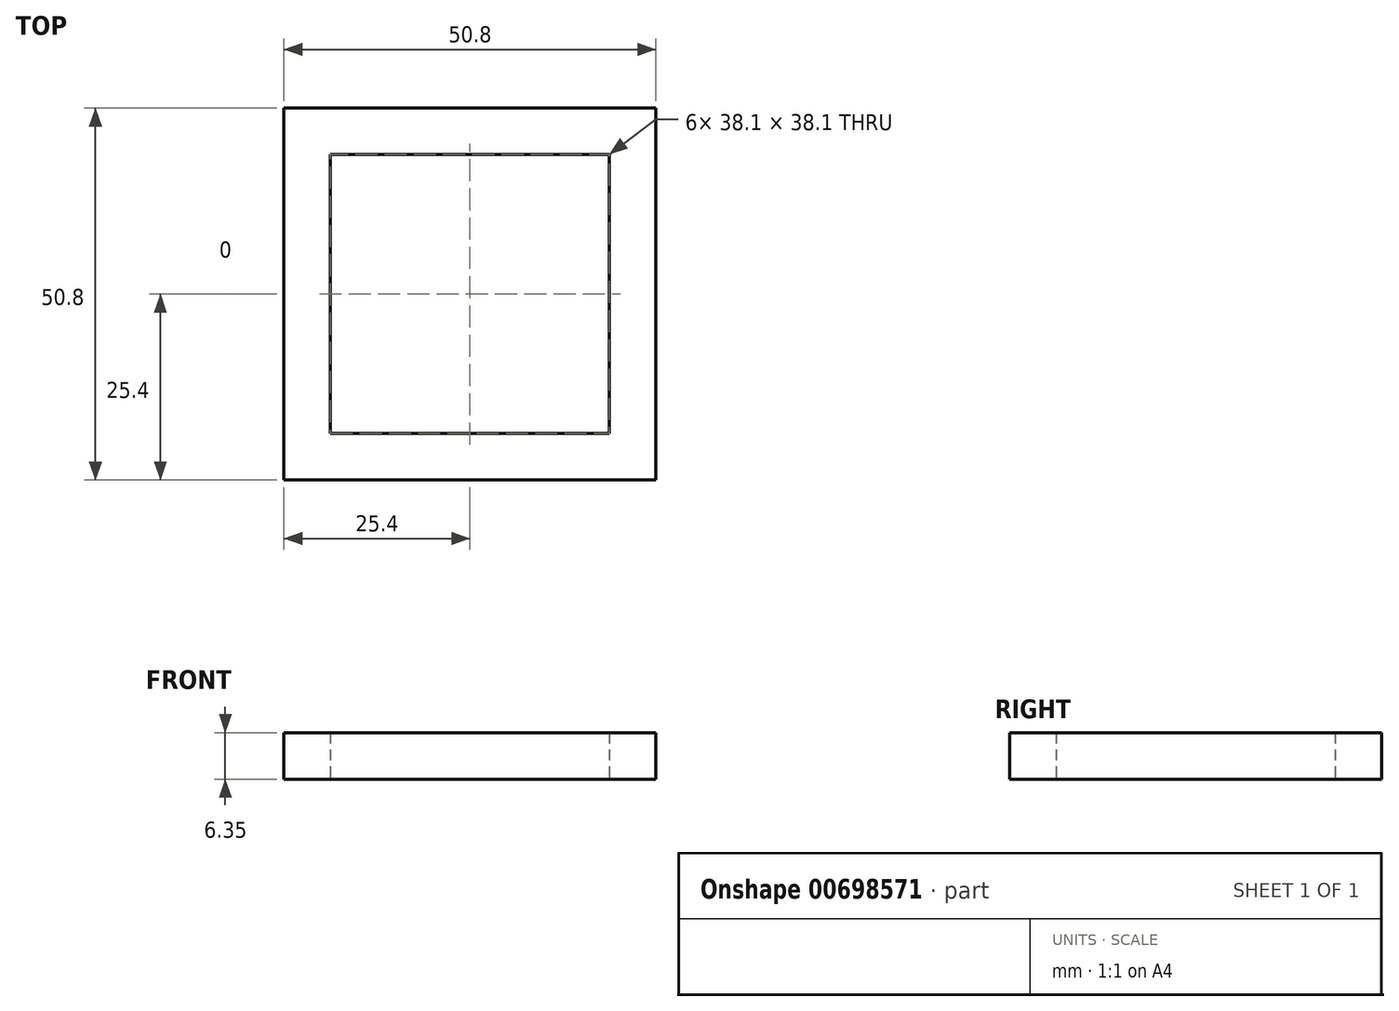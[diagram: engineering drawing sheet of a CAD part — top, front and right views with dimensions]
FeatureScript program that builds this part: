
annotation { "Feature Type Name" : "Feature", "Feature Type Description" : "" }
export const myFeature = defineFeature(function(context is Context, id is Id, definition is map)
    precondition{}
    {
        {
            var Q0;
            Q0=qCreatedBy(makeId("Top.planeOp"),FACE);
            var sketch = newSketch(context, id + "F0", { "sketchPlane" : qUnion([Q0])});
            skLineSegment(sketch, "E0.bottom", {"start": v(0, 0) * mm, "end": v(50.8, 0) * mm});
            skLineSegment(sketch, "E0.top", {"start": v(0, 50.8) * mm, "end": v(50.8, 50.8) * mm});
            skLineSegment(sketch, "E0.left", {"start": v(0, 0) * mm, "end": v(0, 50.8) * mm});
            skLineSegment(sketch, "E0.right", {"start": v(50.8, 0) * mm, "end": v(50.8, 50.8) * mm});
            skLineSegment(sketch, "E1.0", {"start": v(6.35, 44.45) * mm, "end": v(44.45, 44.45) * mm});
            skLineSegment(sketch, "E1.1", {"start": v(6.35, 6.35) * mm, "end": v(6.35, 44.45) * mm});
            skLineSegment(sketch, "E1.2", {"start": v(6.35, 6.35) * mm, "end": v(44.45, 6.35) * mm});
            skLineSegment(sketch, "E1.3", {"start": v(44.45, 6.35) * mm, "end": v(44.45, 44.45) * mm});
            skSolve(sketch);
        }
        {
            var Q0;
            Q0=makeQuery(id+"F0.imprint","IMPRINT",FACE,{"disambiguationData":[TD([[makeQuery(id+"F0.imprint","IMPRINT",EDGE,{"derivedFrom":sQuery(id+"F0.wireOp",EDGE,"E0.bottom")}),1.0]])]});
            extrude(context, id + "F1", {"entities" : qUnion([Q0]), "depth" : 6.35 * mm, "offsetDistance" : 25.4 * mm});
        }
    });
